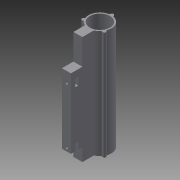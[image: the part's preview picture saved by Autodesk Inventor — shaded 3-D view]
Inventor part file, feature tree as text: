
AUTODESK INVENTOR PART (.ipt)
format: ipt  version: 2013 (Build 170138000, 138)  size: 237,056 bytes
history: native  units: mm
features: sketch x15, extrude x11, hole x3, other x1
ambient origin geometry x8: Origin, YZ Plane, XZ Plane, XY Plane, X Axis, Y Axis, Z Axis, Center Point
feature tree (30):
  other  "ソリッド1"
  extrude  "押し出し1"  Depth=22.0mm
  extrude  "押し出し2"  Depth=25.0mm
  extrude  "押し出し4"  Depth=100.0mm TaperAngle=0.0deg
  hole  "穴1"  [1 undecoded]
  extrude  "押し出し5"  Depth=2.4mm
  extrude  "押し出し6"  Depth=3.0mm
  hole  "穴2"  [1 undecoded]
  extrude  "押し出し11"  Depth=103.0mm TaperAngle=0.0deg
  hole  "穴4"  [1 undecoded]
  extrude  "押し出し13"  Depth=3.0mm TaperAngle=0.0deg
  extrude  "押し出し14"  Depth=11.693706mm
  sketch  "スケッチ16"
  extrude  "押し出し15"  Depth=19.722221mm
  extrude  "押し出し16"  Depth=103.0mm TaperAngle=0.0deg
  extrude  "押し出し17"  Depth=24.5mm
  sketch  "スケッチ1"
  sketch  "スケッチ2"
  sketch  "スケッチ3"
  sketch  "スケッチ4"
  sketch  "スケッチ5"
  sketch  "スケッチ6"
  sketch  "スケッチ7"
  sketch  "スケッチ10"
  sketch  "スケッチ11"
  sketch  "スケッチ13"
  sketch  "スケッチ14"
  sketch  "スケッチ17"
  sketch  "スケッチ18"
  sketch  "スケッチ19"
note: 3 required parameter values undecoded (feature->parameter linkage not recoverable at this tier; creation-order binding heuristic only, values carry confidence <= 0.55)
